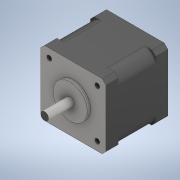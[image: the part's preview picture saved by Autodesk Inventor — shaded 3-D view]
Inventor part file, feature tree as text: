
AUTODESK INVENTOR PART (.ipt)
format: ipt  version: 2022 (Build 260153000, 153)  size: 135,680 bytes
history: mixed  units: in
note: dims shown in document units (in); Inventor stores cm internally (conversion verified against a paired STEP export)
features: extrude x1, sketch x1, imported_body x1
ambient origin geometry x8: Origin, YZ Plane, XZ Plane, XY Plane, X Axis, Y Axis, Z Axis, Center Point
bodies: Solid1 (imported_parasolid), Body1 (imported_parasolid)
feature tree (3):
  extrude  "Extrusion1"  [1 undecoded]
  sketch  "Sketch1"  dims[d0=0.1969in d1=0.0in]
  imported_body  NMx_Import_Brep_tag  [imported B-rep: ~34 faces, bbox_mm=[42.0, 42.0, 58.5]]
note: 1 required parameter value undecoded (feature->parameter linkage not recoverable at this tier; creation-order binding heuristic only, values carry confidence <= 0.55)
